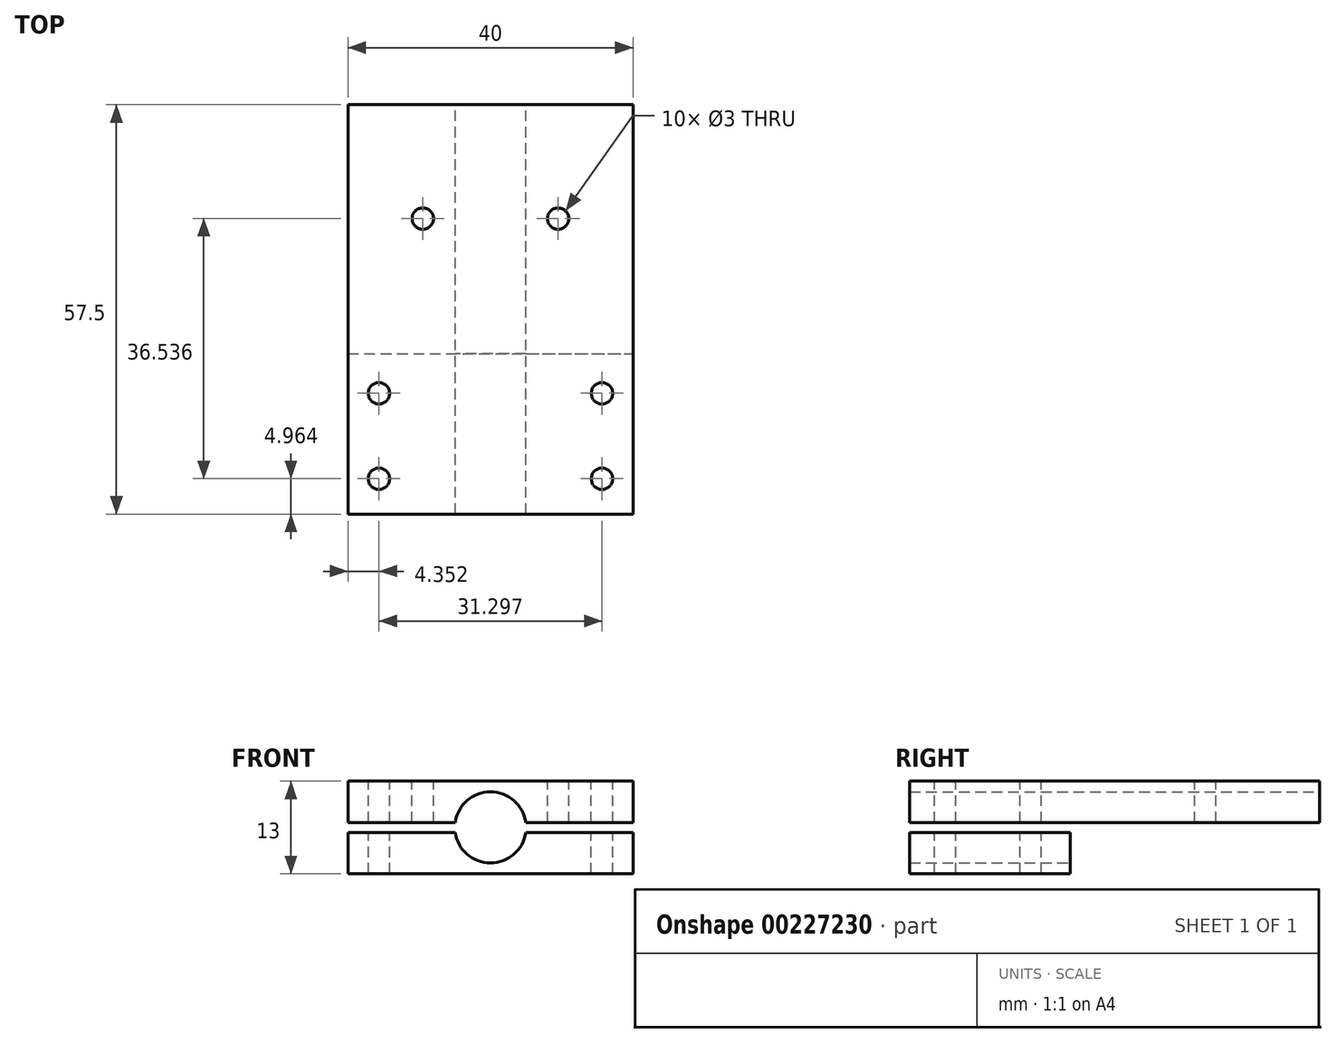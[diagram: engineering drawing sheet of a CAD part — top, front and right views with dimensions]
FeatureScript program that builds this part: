
annotation { "Feature Type Name" : "Feature", "Feature Type Description" : "" }
export const myFeature = defineFeature(function(context is Context, id is Id, definition is map)
    precondition{}
    {
        {
            var Q0;
            Q0=qCreatedBy(makeId("Front.planeOp"),FACE);
            var sketch = newSketch(context, id + "F0", { "sketchPlane" : qUnion([Q0])});
            skArc(sketch, "E0", {"start": v(-4.95, -0.7) * mm, "mid": v(0, -5) * mm, "end": v(4.95, -0.7) * mm});
            skLineSegment(sketch, "E1.bottom", {"start": v(20, -6.5) * mm, "end": v(-20, -6.5) * mm});
            skLineSegment(sketch, "E1.top", {"start": v(20, 6.5) * mm, "end": v(-20, 6.5) * mm});
            skLineSegment(sketch, "E1.left", {"start": v(20, -6.5) * mm, "end": v(20, -0.7) * mm});
            skLineSegment(sketch, "E1.right", {"start": v(-20, -6.5) * mm, "end": v(-20, 6.5) * mm});
            skLineSegment(sketch, "E2.bottom", {"start": v(20, -0.7) * mm, "end": v(4.95, -0.7) * mm});
            skLineSegment(sketch, "E2.top", {"start": v(20, 0.7) * mm, "end": v(4.95, 0.7) * mm});
            skArc(sketch, "E3.trimOffspring", {"start": v(4.95, 0.7) * mm, "mid": v(0, 5) * mm, "end": v(-4.95, 0.7) * mm});
            skLineSegment(sketch, "E4.trimOffspring", {"start": v(-4.95, 0.7) * mm, "end": v(-20, 0.7) * mm});
            skLineSegment(sketch, "E5.trimOffspring", {"start": v(-4.95, -0.7) * mm, "end": v(-20, -0.7) * mm});
            skLineSegment(sketch, "E6.trimOffspring", {"start": v(20, 0.7) * mm, "end": v(20, 6.5) * mm});
            skSolve(sketch);
        }
        {
            var Q0;
            Q0 = qSketchRegion(id + "F0", true);
            extrude(context, id + "F1", {"entities" : qUnion([Q0]), "depth" : 45 * mm});
        }
        {
            var Q0;
            Q0=makeQuery(id+"F1.opExtrude","SWEPT_FACE",FACE,{"disambiguationData":[OSD([sQuery(id+"F0.wireOp",EDGE,"E1.top")])]});
            var sketch = newSketch(context, id + "F2", { "sketchPlane" : qUnion([Q0])});
            skLineSegment(sketch, "E7", {"start": v(20, -22.5) * mm, "end": v(-20, -22.5) * mm});
            skSolve(sketch);
        }
        {
            var Q0;
            {var subQ0=sQuery(id+"F2.wireOp",EDGE,"E7");Q0=makeQuery(id+"F2.imprint","IMPRINT",FACE,{"disambiguationData":[TD([[makeQuery(id+"F2.imprint","IMPRINT",EDGE,{"derivedFrom":subQ0}),-1.0]])]});}
            extrude(context, id + "F3", {"entities" : qUnion([Q0]), "operationType" : NewBodyOperationType.REMOVE, "oppositeDirection" : true, "depth" : 25 * mm});
        }
        {
            var Q0;
            {var subQ1=sQuery(id+"F0.wireOp",EDGE,"E1.top");Q0=makeQuery(id+"F3.boolean.opBoolean","COPY",FACE,{"disambiguationData":[TD([makeQuery(id+"F1.opExtrude","SWEPT_FACE",FACE,{"disambiguationData":[OSD([subQ1])]})])],"derivedFrom":makeQuery(id+"F3.opExtrude","SWEPT_FACE",FACE,{"disambiguationData":[OSD([sQuery(id+"F2.wireOp",EDGE,"E7")])]})});}
            var sketch = newSketch(context, id + "F4", { "sketchPlane" : qUnion([Q0])});
            skLineSegment(sketch, "E8.bottom", {"start": v(-20, 6.5) * mm, "end": v(20, 6.5) * mm});
            skLineSegment(sketch, "E8.top", {"start": v(-20, 0.7) * mm, "end": v(20, 0.7) * mm});
            skLineSegment(sketch, "E8.left", {"start": v(-20, 6.5) * mm, "end": v(-20, 0.7) * mm});
            skLineSegment(sketch, "E8.right", {"start": v(20, 6.5) * mm, "end": v(20, 0.7) * mm});
            skSolve(sketch);
        }
        {
            var Q0;
            Q0=makeQuery(id+"F3.boolean.opBoolean","COPY",FACE,{"disambiguationData":[TD([makeQuery(id+"F1.opExtrude","SWEPT_FACE",FACE,{"disambiguationData":[OSD([sQuery(id+"F0.wireOp",EDGE,"E0")])]})])],"derivedFrom":makeQuery(id+"F3.opExtrude","SWEPT_FACE",FACE,{"disambiguationData":[OSD([sQuery(id+"F2.wireOp",EDGE,"E7")])]})});
            var sketch = newSketch(context, id + "F5", { "sketchPlane" : qUnion([Q0])});
            skLineSegment(sketch, "E9.bottom", {"start": v(-20, -0.7) * mm, "end": v(20, -0.7) * mm});
            skLineSegment(sketch, "E9.top", {"start": v(-20, -6.5) * mm, "end": v(20, -6.5) * mm});
            skLineSegment(sketch, "E9.left", {"start": v(-20, -0.7) * mm, "end": v(-20, -6.5) * mm});
            skLineSegment(sketch, "E9.right", {"start": v(20, -0.7) * mm, "end": v(20, -6.5) * mm});
            skSolve(sketch);
        }
        {
            var Q0;
            Q0 = qSketchRegion(id + "F4", true);
            var Q1;
            Q1 = qSketchRegion(id + "F5", true);
            extrude(context, id + "F6", {"entities" : qUnion([Q0, Q1]), "depth" : 25 * mm});
        }
        {
            var Q0;
            Q0=makeQuery(id+"F1.opExtrude","SWEPT_BODY",BODY,{"disambiguationData":[OSD([sQuery(id+"F0.wireOp",EDGE,"E1.top"),sQuery(id+"F0.wireOp",EDGE,"E1.right"),sQuery(id+"F0.wireOp",EDGE,"E2.top"),sQuery(id+"F0.wireOp",EDGE,"E3.trimOffspring"),sQuery(id+"F0.wireOp",EDGE,"E4.trimOffspring"),sQuery(id+"F0.wireOp",EDGE,"E6.trimOffspring")])]});
            var Q1;
            Q1=makeQuery(id+"F6.opExtrude","SWEPT_BODY",BODY,{"disambiguationData":[OSD([sQuery(id+"F4.wireOp",EDGE,"E8.bottom"),sQuery(id+"F4.wireOp",EDGE,"E8.top"),sQuery(id+"F4.wireOp",EDGE,"E8.left"),sQuery(id+"F4.wireOp",EDGE,"E8.right")])]});
            booleanBodies(context, id + "F7", {"operationType" : BooleanOperationType.UNION, "tools" : qUnion([Q0, Q1])});
        }
        {
            var Q0;
            Q0=makeQuery(id+"F6.opExtrude","CAP_FACE",FACE,{"disambiguationData":[OSD([sQuery(id+"F4.wireOp",EDGE,"E8.bottom"),sQuery(id+"F4.wireOp",EDGE,"E8.top"),sQuery(id+"F4.wireOp",EDGE,"E8.left"),sQuery(id+"F4.wireOp",EDGE,"E8.right")])],"isStart":false});
            var Q1;
            Q1=makeQuery(id+"F6.opExtrude","CAP_FACE",FACE,{"disambiguationData":[OSD([sQuery(id+"F5.wireOp",EDGE,"E9.bottom"),sQuery(id+"F5.wireOp",EDGE,"E9.top"),sQuery(id+"F5.wireOp",EDGE,"E9.left"),sQuery(id+"F5.wireOp",EDGE,"E9.right")])],"isStart":false});
            extrude(context, id + "F8", {"entities" : qUnion([Q0, Q1]), "operationType" : NewBodyOperationType.ADD, "depth" : 10 * mm});
        }
        {
            var Q0;
            Q0=makeQuery(id+"F7.opBoolean","MERGE",FACE,{"derivedFrom":[makeQuery(id+"F1.opExtrude","SWEPT_FACE",FACE,{"disambiguationData":[OSD([sQuery(id+"F0.wireOp",EDGE,"E1.top")])]}),makeQuery(id+"F6.opExtrude","SWEPT_FACE",FACE,{"disambiguationData":[OSD([sQuery(id+"F4.wireOp",EDGE,"E8.bottom")])]})]});
            var sketch = newSketch(context, id + "F9", { "sketchPlane" : qUnion([Q0])});
            skLineSegment(sketch, "E10.direction1", {"start": v(0, 6) * mm, "end": v(25, 6) * mm, "construction": true});
            skLineSegment(sketch, "E10.direction2", {"start": v(0, 6) * mm, "end": v(0, -13) * mm, "construction": true});
            skCircle(sketch, "E11", {"center": v(-15.65, -40.04) * mm, "radius": 1.5 * mm});
            skCircle(sketch, "E12.0.1.0", {"center": v(-15.65, -28.04) * mm, "radius": 1.5 * mm});
            skLineSegment(sketch, "E12.direction1", {"start": v(-15.65, -40.04) * mm, "end": v(9.35, -40.04) * mm, "construction": true});
            skLineSegment(sketch, "E12.direction2", {"start": v(-15.65, -40.04) * mm, "end": v(-15.65, -28.04) * mm, "construction": true});
            skCircle(sketch, "E13.MirrorC", {"center": v(15.65, -40.04) * mm, "radius": 1.5 * mm});
            skCircle(sketch, "E14.MirrorC", {"center": v(15.65, -28.04) * mm, "radius": 1.5 * mm});
            skCircle(sketch, "E15.1.0", {"center": v(9.5, -3.5) * mm, "radius": 1.5 * mm});
            skCircle(sketch, "E15.1.1", {"center": v(-9.5, -3.5) * mm, "radius": 1.5 * mm});
            skPoint(sketch, "E15.center", {"position": v(0, -3.5) * mm});
            skSolve(sketch);
        }
        {
            var Q0;
            Q0 = qSketchRegion(id + "F9", true);
            extrude(context, id + "F10", {"entities" : qUnion([Q0]), "operationType" : NewBodyOperationType.REMOVE, "oppositeDirection" : true, "depth" : 25 * mm});
        }
        {
            var Q0;
            Q0=makeQuery(id+"F6.opExtrude","CAP_FACE",FACE,{"disambiguationData":[OSD([sQuery(id+"F4.wireOp",EDGE,"E8.bottom"),sQuery(id+"F4.wireOp",EDGE,"E8.top"),sQuery(id+"F4.wireOp",EDGE,"E8.left"),sQuery(id+"F4.wireOp",EDGE,"E8.right")])],"isStart":true});
            var Q1;
            Q1=makeQuery(id+"F6.opExtrude","CAP_FACE",FACE,{"disambiguationData":[OSD([sQuery(id+"F5.wireOp",EDGE,"E9.bottom"),sQuery(id+"F5.wireOp",EDGE,"E9.top"),sQuery(id+"F5.wireOp",EDGE,"E9.left"),sQuery(id+"F5.wireOp",EDGE,"E9.right")])],"isStart":true});
            extrude(context, id + "F11", {"entities" : qUnion([Q0, Q1]), "operationType" : NewBodyOperationType.REMOVE, "oppositeDirection" : true, "depth" : 56.4 * mm});
        }
    });
